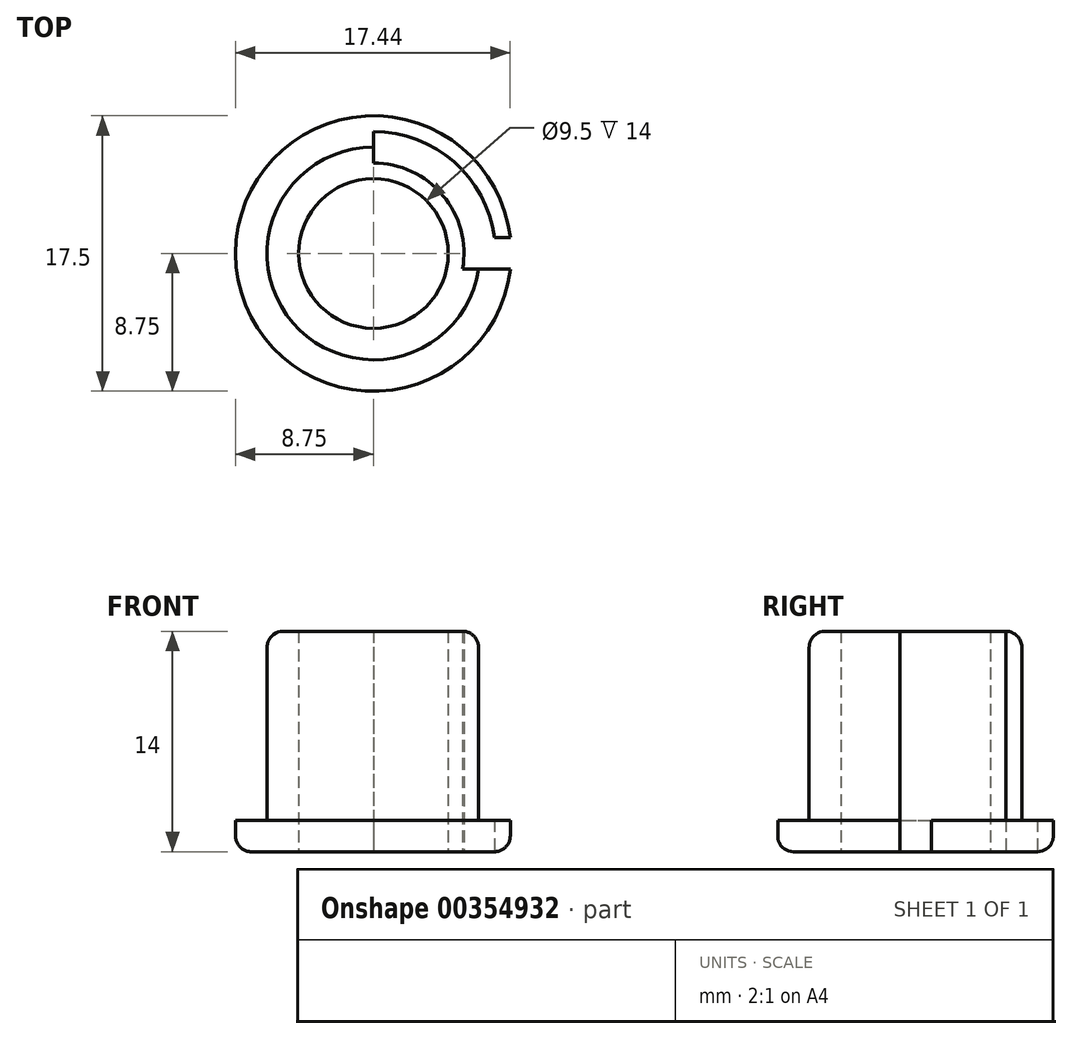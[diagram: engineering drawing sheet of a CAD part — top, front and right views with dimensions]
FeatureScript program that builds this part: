
annotation { "Feature Type Name" : "Feature", "Feature Type Description" : "" }
export const myFeature = defineFeature(function(context is Context, id is Id, definition is map)
    precondition{}
    {
        {
            var Q0;
            Q0=qCreatedBy(makeId("Top.planeOp"),FACE);
            var sketch = newSketch(context, id + "F0", { "sketchPlane" : qUnion([Q0])});
            skCircle(sketch, "E0", {"center": v(0, 0) * mm, "radius": 6.75 * mm});
            skSolve(sketch);
        }
        {
            var Q0;
            Q0 = qSketchRegion(id + "F0", true);
            extrude(context, id + "F1", {"entities" : qUnion([Q0]), "depth" : 14 * mm});
        }
        {
            var Q0;
            Q0=makeQuery(id+"F1.opExtrude","CAP_FACE",FACE,{"disambiguationData":[OSD([sQuery(id+"F0.wireOp",EDGE,"E0")])],"isStart":true});
            var sketch = newSketch(context, id + "F2", { "sketchPlane" : qUnion([Q0])});
            skCircle(sketch, "E1.0", {"center": v(0, 0) * mm, "radius": 6.75 * mm});
            skCircle(sketch, "E2.0", {"center": v(0, 0) * mm, "radius": 8.75 * mm});
            skSolve(sketch);
        }
        {
            var Q0;
            Q0 = qSketchRegion(id + "F2", true);
            extrude(context, id + "F3", {"entities" : qUnion([Q0]), "operationType" : NewBodyOperationType.ADD, "oppositeDirection" : true, "depth" : 2 * mm});
        }
        {
            var Q0;
            Q0=makeQuery(id+"F3.boolean.opBoolean","MERGE",FACE,{"derivedFrom":[makeQuery(id+"F1.opExtrude","CAP_FACE",FACE,{"disambiguationData":[OSD([sQuery(id+"F0.wireOp",EDGE,"E0")])],"isStart":true}),makeQuery(id+"F3.opExtrude","CAP_FACE",FACE,{"disambiguationData":[OSD([sQuery(id+"F2.wireOp",EDGE,"E1.0"),sQuery(id+"F2.wireOp",EDGE,"E2.0")])],"isStart":true})]});
            var sketch = newSketch(context, id + "F4", { "sketchPlane" : qUnion([Q0])});
            skCircle(sketch, "E3.0", {"center": v(0, 0) * mm, "radius": 6.75 * mm});
            skCircle(sketch, "E4.0", {"center": v(0, 0) * mm, "radius": 4.75 * mm});
            skSolve(sketch);
        }
        {
            var Q0;
            Q0=makeQuery(id+"F4.imprint","IMPRINT",FACE,{"disambiguationData":[TD([[makeQuery(id+"F4.imprint","IMPRINT",EDGE,{"derivedFrom":sQuery(id+"F4.wireOp",EDGE,"E4.0")}),1.0]])]});
            var Q1;
            Q1=makeQuery(id+"F1.opExtrude","CAP_FACE",FACE,{"disambiguationData":[OSD([sQuery(id+"F0.wireOp",EDGE,"E0")])],"isStart":false});
            extrude(context, id + "F5", {"entities" : qUnion([Q0]), "operationType" : NewBodyOperationType.REMOVE, "endBound" : BoundingType.UP_TO_SURFACE, "oppositeDirection" : true, "endBoundEntityFace" : qUnion([Q1]), "depth" : 25 * mm});
        }
        {
            var Q0;
            Q0=makeQuery(id+"F1.opExtrude","CAP_EDGE",EDGE,{"disambiguationData":[OSD([sQuery(id+"F0.wireOp",EDGE,"E0")])],"isStart":false});
            fillet(context, id + "F6", {"entities" : qUnion([Q0]), "radius" : 1 * mm, "tangentPropagation" : true, "allowEdgeOverflow" : false});
        }
        {
            var Q0;
            Q0=makeQuery(id+"F5.boolean.opBoolean","COPY",EDGE,{"derivedFrom":makeQuery(id+"F5.opExtrude","CAP_EDGE",EDGE,{"disambiguationData":[OSD([sQuery(id+"F4.wireOp",EDGE,"E4.0")])],"isStart":true})});
            var Q1;
            Q1=makeQuery(id+"F3.opExtrude","CAP_EDGE",EDGE,{"disambiguationData":[OSD([sQuery(id+"F2.wireOp",EDGE,"E2.0")])],"isStart":true});
            var Q2;
            Q2=makeQuery(id+"F5.boolean.opBoolean","COPY",EDGE,{"derivedFrom":makeQuery(id+"F5.opExtrude","CAP_EDGE",EDGE,{"disambiguationData":[OSD([sQuery(id+"F4.wireOp",EDGE,"E4.0")])],"isStart":false})});
            fillet(context, id + "F7", {"entities" : qUnion([Q0, Q1, Q2]), "radius" : 1 * mm, "tangentPropagation" : true, "allowEdgeOverflow" : false});
        }
        {
            var Q0;
            Q0=makeQuery(id+"F3.boolean.opBoolean","MERGE",FACE,{"derivedFrom":[makeQuery(id+"F1.opExtrude","CAP_FACE",FACE,{"disambiguationData":[OSD([sQuery(id+"F0.wireOp",EDGE,"E0")])],"isStart":true}),makeQuery(id+"F3.opExtrude","CAP_FACE",FACE,{"disambiguationData":[OSD([sQuery(id+"F2.wireOp",EDGE,"E1.0"),sQuery(id+"F2.wireOp",EDGE,"E2.0")])],"isStart":true})]});
            var sketch = newSketch(context, id + "F8", { "sketchPlane" : qUnion([Q0])});
            skCircle(sketch, "E5.0.0", {"center": v(0, 0) * mm, "radius": 7.75 * mm});
            skCircle(sketch, "E6.0", {"center": v(0, 0) * mm, "radius": 5.75 * mm});
            skLineSegment(sketch, "E7.bottom", {"start": v(-20, 20) * mm, "end": v(20, 20) * mm});
            skLineSegment(sketch, "E7.top", {"start": v(-20, -20) * mm, "end": v(20, -20) * mm});
            skLineSegment(sketch, "E7.left", {"start": v(-20, 20) * mm, "end": v(-20, -20) * mm});
            skLineSegment(sketch, "E7.right", {"start": v(20, 20) * mm, "end": v(20, -20) * mm});
            skLineSegment(sketch, "E8", {"start": v(0, 20) * mm, "end": v(0, -20) * mm});
            skLineSegment(sketch, "E9", {"start": v(-20, 0) * mm, "end": v(20, 0) * mm});
            skLineSegment(sketch, "E10.0", {"start": v(-20, -1) * mm, "end": v(20, -1) * mm});
            skLineSegment(sketch, "E11.MirrorCS", {"start": v(-20, 1) * mm, "end": v(20, 1) * mm});
            skSolve(sketch);
        }
        {
            var Q0;
            {var subQ0=sQuery(id+"F8.wireOp",EDGE,"E9");var subQ1=sQuery(id+"F8.wireOp",EDGE,"E6.0");var subQ2=makeQuery(id+"F8.imprint","INTERSECT",VERTEX,{"disambiguationData":[OD(0.0)],"derivedFrom":[subQ1,subQ0]});Q0=makeQuery(id+"F8.imprint","IMPRINT",FACE,{"disambiguationData":[TD([[makeQuery(id+"F8.imprint","IMPRINT",EDGE,{"disambiguationData":[TD([[subQ2,1.0]])],"derivedFrom":subQ1}),-1.0]])]});}
            var Q1;
            {var subQ0=sQuery(id+"F8.wireOp",EDGE,"E10.0");var subQ1=sQuery(id+"F8.wireOp",EDGE,"E6.0");var subQ2=makeQuery(id+"F8.imprint","INTERSECT",VERTEX,{"disambiguationData":[OD(0.0)],"derivedFrom":[subQ1,subQ0]});Q1=makeQuery(id+"F8.imprint","IMPRINT",FACE,{"disambiguationData":[TD([[makeQuery(id+"F8.imprint","IMPRINT",EDGE,{"disambiguationData":[TD([[subQ2,1.0]])],"derivedFrom":subQ1}),-1.0]])]});}
            var Q2;
            {var subQ0=sQuery(id+"F8.wireOp",EDGE,"E9");var subQ1=sQuery(id+"F8.wireOp",EDGE,"E5.0.0");var subQ2=makeQuery(id+"F8.imprint","INTERSECT",VERTEX,{"disambiguationData":[OD(0.0)],"derivedFrom":[subQ1,subQ0]});Q2=makeQuery(id+"F8.imprint","IMPRINT",FACE,{"disambiguationData":[TD([[makeQuery(id+"F8.imprint","IMPRINT",EDGE,{"disambiguationData":[TD([[subQ2,-1.0]])],"derivedFrom":subQ1}),1.0]])]});}
            var Q3;
            {var subQ0=sQuery(id+"F8.wireOp",EDGE,"E10.0");var subQ1=sQuery(id+"F8.wireOp",EDGE,"E5.0.0");var subQ2=makeQuery(id+"F8.imprint","INTERSECT",VERTEX,{"disambiguationData":[OD(0.0)],"derivedFrom":[subQ1,subQ0]});Q3=makeQuery(id+"F8.imprint","IMPRINT",FACE,{"disambiguationData":[TD([[makeQuery(id+"F8.imprint","IMPRINT",EDGE,{"disambiguationData":[TD([[subQ2,-1.0]])],"derivedFrom":subQ1}),1.0]])]});}
            var Q4;
            {var subQ0=sQuery(id+"F8.wireOp",EDGE,"E9");var subQ1=sQuery(id+"F8.wireOp",EDGE,"E5.0.0");var subQ2=makeQuery(id+"F8.imprint","INTERSECT",VERTEX,{"disambiguationData":[OD(0.0)],"derivedFrom":[subQ1,subQ0]});Q4=makeQuery(id+"F8.imprint","IMPRINT",FACE,{"disambiguationData":[TD([[makeQuery(id+"F8.imprint","IMPRINT",EDGE,{"disambiguationData":[TD([[subQ2,-1.0]])],"derivedFrom":subQ1}),-1.0]])]});}
            var Q5;
            {var subQ0=sQuery(id+"F8.wireOp",EDGE,"E10.0");var subQ1=sQuery(id+"F8.wireOp",EDGE,"E5.0.0");var subQ2=makeQuery(id+"F8.imprint","INTERSECT",VERTEX,{"disambiguationData":[OD(0.0)],"derivedFrom":[subQ1,subQ0]});Q5=makeQuery(id+"F8.imprint","IMPRINT",FACE,{"disambiguationData":[TD([[makeQuery(id+"F8.imprint","IMPRINT",EDGE,{"disambiguationData":[TD([[subQ2,-1.0]])],"derivedFrom":subQ1}),-1.0]])]});}
            var Q6;
            Q6=makeQuery(id+"F6.opFillet","BLEND_FACE",FACE,{"disambiguationData":[OSD([sQuery(id+"F0.wireOp",EDGE,"E0")])]});
            extrude(context, id + "F9", {"entities" : qUnion([Q0, Q1, Q2, Q3, Q4, Q5]), "operationType" : NewBodyOperationType.REMOVE, "oppositeDirection" : true, "endBoundEntityFace" : qUnion([Q6]), "depth" : 20 * mm});
        }
    });
